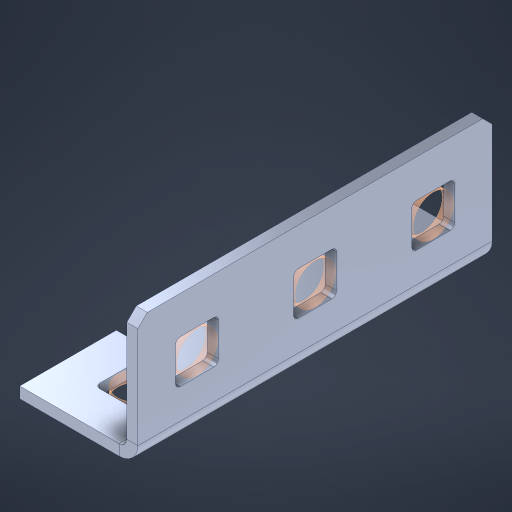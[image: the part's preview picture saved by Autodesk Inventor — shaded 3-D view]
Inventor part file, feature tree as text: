
AUTODESK INVENTOR PART (.ipt)
format: ipt  version: 2023 (Build 270158000, 158)  size: 515,072 bytes
history: native  units: in
note: dims shown in document units (in); Inventor stores cm internally (conversion verified against a paired STEP export)
features: other x16, sheet_metal_op x11, sketch x10, extrude x7, pattern_linear x2, mirror x1, chamfer x1
ambient origin geometry x8: Origin, YZ Plane, XZ Plane, XY Plane, X Axis, Y Axis, Z Axis, Center Point
bodies: Solid1 (feature_tree), Body (feature_tree)
feature tree (48):
  sheet_metal_op  "Flanges"
  other  "Flange Pattern Plane"
  other  "Flange Pattern Sketch"
  sheet_metal_op  "Flange Pattern"
  sheet_metal_op  "Body Pattern"
  pattern_linear  "Center Pattern"  Spacing1=0.0469in  [1 undecoded]
  other  "Arc Length"
  mirror  "Notch Mirror"
  pattern_linear  "Notch Pattern"  Spacing1=0.182in  [1 undecoded]
  chamfer  "End Chamfer"
  extrude  "Half Cut"  Depth=0.02in
  sketch  "Sketch1"  dims[d0=1.0in]
  other  "Plate1"
  sketch  "Sketch2"  dims[d1=1.5in]
  other  "Plate2"
  sheet_metal_op  "Bend1"
  sheet_metal_op  "Corner1"
  sketch  "Sketch3"  dims[d2=0.0469in]
  sketch  "Sketch7"  dims[d3=0.0469in]
  other  "Srf1"
  other  "Srf2"
  sketch  "Sketch8"  dims[d4=0.0234in]
  sketch  "Sketch9"  dims[d5=0.0938in]
  other  "Srf91"
  sheet_metal_op  "Body Pattern Sketch"
  other  "Srf92"
  sketch  "Sketch13"  dims[d6=0.0469in]
  sketch  "Sketch14"  dims[d7=0.5in d8=90.0deg d9=0.0312in]
  sketch  "Sketch15"  dims[d10=0.1875in]
  sketch  "Sketch16"  dims[d11=0.0469in d12=0.0469in d16=0.182in d17=0.02in d18=0.0469in d19=0.0in d20=0.25in d21=0.25in d38=1.1811in d40=0.5in d41=0.3937in d43=1.0in d46=0.172in d47=1.0in d48=0.0in d49=0.182in d50=0.02in d51=0.25in d52=0.25in d53=0.0469in d54=0.0in d55=0.172in d56=1.0in d57=0.0in d58=0.25in d60=1.1811in d62=0.5in d63=0.3937in d65=0.5in d85=0.1227in d86=0.1659in d88=0.04in d89=0.0469in d90=0.0in d91=0.04in d92=0.0491in d95=2.5in d96=0.04in d97=0.25in d98=45.0deg d99=0.25in d100=0.5in d101=0.0in d102=2.497in d106=0.182in d107=0.02in d108=0.5in d109=0.5in d110=0.0469in d111=0.0in d112=0.172in d113=0.5in d114=0.0in d117=0.5in d118=0.5in d119=0.5in]
  other  "Srf786"
  other  "Srf823"
  other  "Srf856"
  other  "Srf889"
  other  "Srf890"
  sheet_metal_op  "Flange Stamp"
  sheet_metal_op  "Flange Circle"
  sheet_metal_op  "Body Stamp"
  sheet_metal_op  "Body Circle"
  other  "Center Stamp"
  other  "Center Circle"
  sheet_metal_op  "Notch"
  extrude  "ExtrusionSrf2"  Depth=0.0469in
  extrude  "ExtrusionSrf92"  TaperAngle=0.0deg  [1 undecoded]
  extrude  "ExtrusionSrf823"  Depth=0.25in
  extrude  "ExtrusionSrf856"  Depth=0.25in
  extrude  "ExtrusionSrf889"  Depth=0.5in
  extrude  "ExtrusionSrf890"  Depth=0.5in
note: 3 required parameter values undecoded (feature->parameter linkage not recoverable at this tier; creation-order binding heuristic only, values carry confidence <= 0.55)
